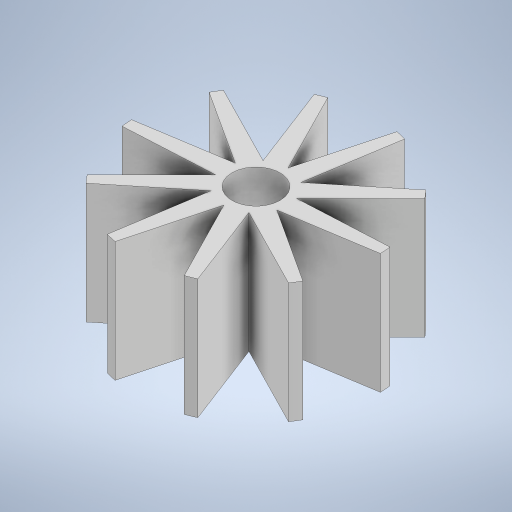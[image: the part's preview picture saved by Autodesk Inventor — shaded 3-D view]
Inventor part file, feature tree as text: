
AUTODESK INVENTOR PART (.ipt)
format: ipt  version: 2024 (Build 280153000, 153)  size: 268,288 bytes
history: native  units: mm
features: extrude x2, sketch x2
ambient origin geometry x8: Origin, YZ Plane, XZ Plane, XY Plane, X Axis, Y Axis, Z Axis, Center Point
bodies: Solid1 (feature_tree)
feature tree (4):
  extrude  "Extrusion1"  Depth=10.0mm TaperAngle=360.0deg
  extrude  "Extrusion2"  Depth=5.0mm
  sketch  "Sketch1"  dims[d0=10.0mm d1=100.0mm d3=360.0deg]
  sketch  "Sketch2"  dims[d5=5.0mm d6=0.0mm d7=2.0mm d8=5.0mm d9=0.0mm]
